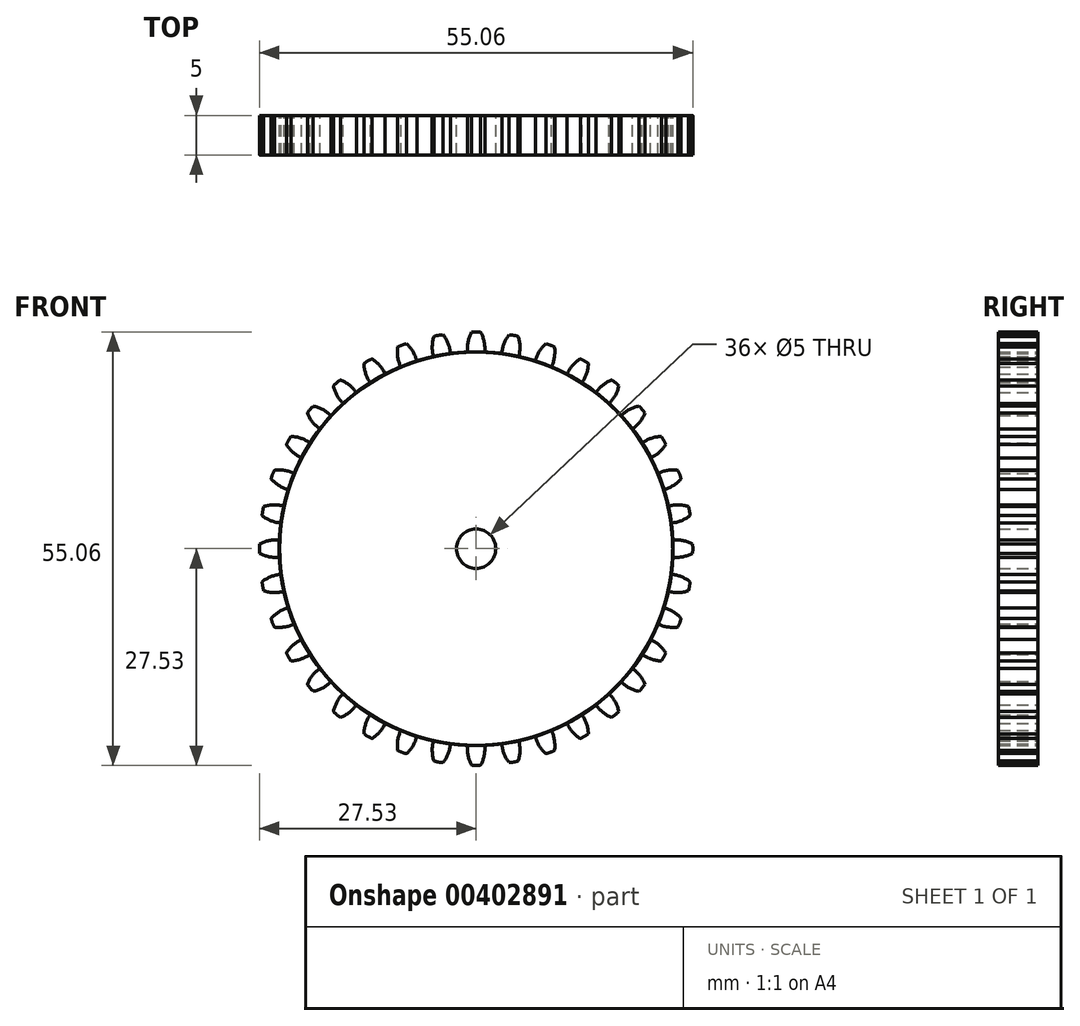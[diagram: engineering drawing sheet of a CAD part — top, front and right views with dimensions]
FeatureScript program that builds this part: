
annotation { "Feature Type Name" : "Feature", "Feature Type Description" : "" }
export const myFeature = defineFeature(function(context is Context, id is Id, definition is map)
    precondition{}
    {
        {
            var Q0;
            Q0=qCreatedBy(makeId("Front.planeOp"),FACE);
            var sketch = newSketch(context, id + "F0", { "sketchPlane" : qUnion([Q0])});
            skCircle(sketch, "E0", {"center": v(0, 0) * mm, "radius": 25 * mm});
            skLineSegment(sketch, "E1", {"start": v(0, 0) * mm, "end": v(0, 2) * mm, "construction": true});
            skLineSegment(sketch, "E2", {"start": v(0, 0) * mm, "end": v(-1.48, 33.99) * mm, "construction": true});
            skLineSegment(sketch, "E3.MirrorCS", {"start": v(0, 0) * mm, "end": v(1.48, 33.99) * mm, "construction": true});
            skArc(sketch, "E4", {"start": v(-0.59, 27.5) * mm, "mid": v(-1.03, 26.27) * mm, "end": v(-1.1, 24.98) * mm});
            skArc(sketch, "E5.MirrorCS", {"start": v(0.59, 27.5) * mm, "mid": v(1.03, 26.27) * mm, "end": v(1.1, 24.98) * mm});
            skArc(sketch, "E6", {"start": v(0.59, 27.5) * mm, "mid": v(0, 27.53) * mm, "end": v(-0.59, 27.5) * mm});
            skCircle(sketch, "E7", {"center": v(0, 0) * mm, "radius": 2.5 * mm});
            skSolve(sketch);
        }
        {
            var Q0;
            Q0 = qSketchRegion(id + "F0", true);
            extrude(context, id + "F1", {"entities" : qUnion([Q0]), "depth" : 5 * mm});
        }
        {
            var Q0;
            Q0=makeQuery(id+"F1.opExtrude","SWEPT_BODY",BODY,{"disambiguationData":[OSD([sQuery(id+"F0.wireOp",EDGE,"E0"),sQuery(id+"F0.wireOp",EDGE,"E4"),sQuery(id+"F0.wireOp",EDGE,"E5.MirrorCS"),sQuery(id+"F0.wireOp",EDGE,"E6")])]});
            var Q1;
            Q1=makeQuery(id+"F1.opExtrude","SWEPT_FACE",FACE,{"disambiguationData":[OSD([sQuery(id+"F0.wireOp",EDGE,"E0")])]});
            circularPattern(context, id + "F2", {"entities" : qUnion([Q0]), "axis" : qUnion([Q1]), "angle" : 360 * degree, "instanceCount" : 36, "equalSpace" : true});
        }
    });
